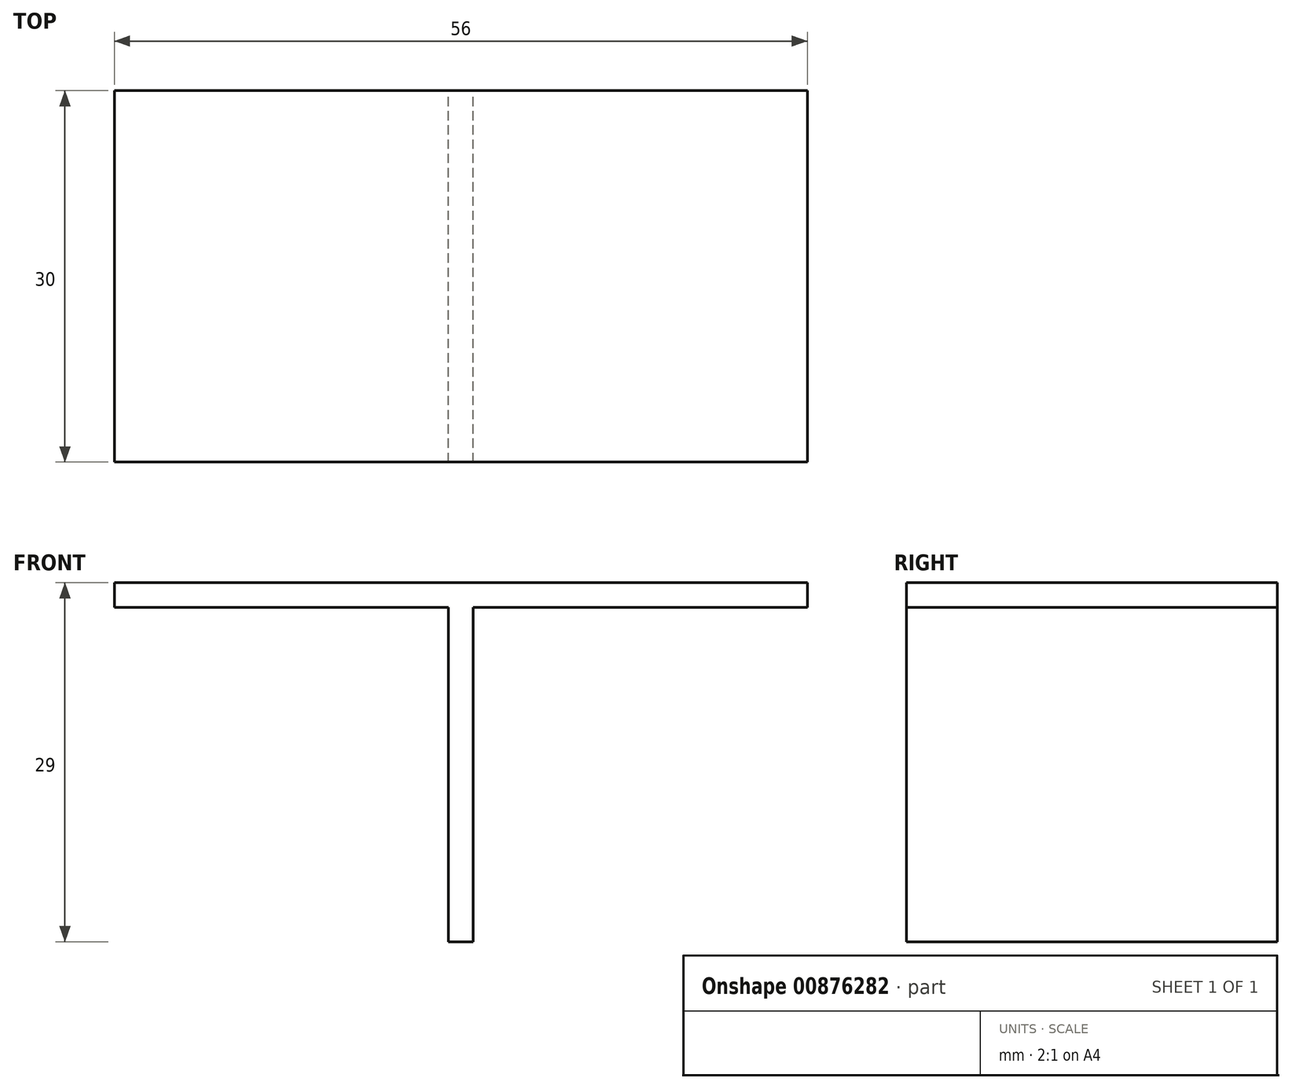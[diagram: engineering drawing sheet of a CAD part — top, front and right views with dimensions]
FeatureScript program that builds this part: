
annotation { "Feature Type Name" : "Feature", "Feature Type Description" : "" }
export const myFeature = defineFeature(function(context is Context, id is Id, definition is map)
    precondition{}
    {
        {
            var Q0;
            Q0=qCreatedBy(makeId("Front.planeOp"),FACE);
            var sketch = newSketch(context, id + "F0", { "sketchPlane" : qUnion([Q0])});
            skLineSegment(sketch, "E0", {"start": v(0, 0) * mm, "end": v(28, 0) * mm});
            skLineSegment(sketch, "E1", {"start": v(28, 0) * mm, "end": v(28, -29) * mm, "construction": true});
            skLineSegment(sketch, "E2", {"start": v(28, -29) * mm, "end": v(27, -29) * mm});
            skLineSegment(sketch, "E3", {"start": v(27, -29) * mm, "end": v(27, -2) * mm});
            skLineSegment(sketch, "E4", {"start": v(27, -2) * mm, "end": v(0, -2) * mm});
            skLineSegment(sketch, "E5", {"start": v(0, -2) * mm, "end": v(0, 0) * mm});
            skLineSegment(sketch, "E6.MirrorCS", {"start": v(56, 0) * mm, "end": v(28, 0) * mm});
            skLineSegment(sketch, "E7.MirrorCS", {"start": v(56, -2) * mm, "end": v(56, 0) * mm});
            skLineSegment(sketch, "E8.MirrorCS", {"start": v(29, -2) * mm, "end": v(56, -2) * mm});
            skLineSegment(sketch, "E9.MirrorCS", {"start": v(29, -29) * mm, "end": v(29, -2) * mm});
            skLineSegment(sketch, "E10.MirrorCS", {"start": v(28, -29) * mm, "end": v(29, -29) * mm});
            skSolve(sketch);
        }
        {
            var Q0;
            Q0=makeQuery(id+"F0.imprint","IMPRINT",FACE,{"disambiguationData":[TD([[makeQuery(id+"F0.imprint","IMPRINT",EDGE,{"derivedFrom":sQuery(id+"F0.wireOp",EDGE,"E0")}),-1.0]])]});
            extrude(context, id + "F1", {"entities" : qUnion([Q0]), "depth" : 30 * mm, "offsetDistance" : 25.4 * mm});
        }
    });
